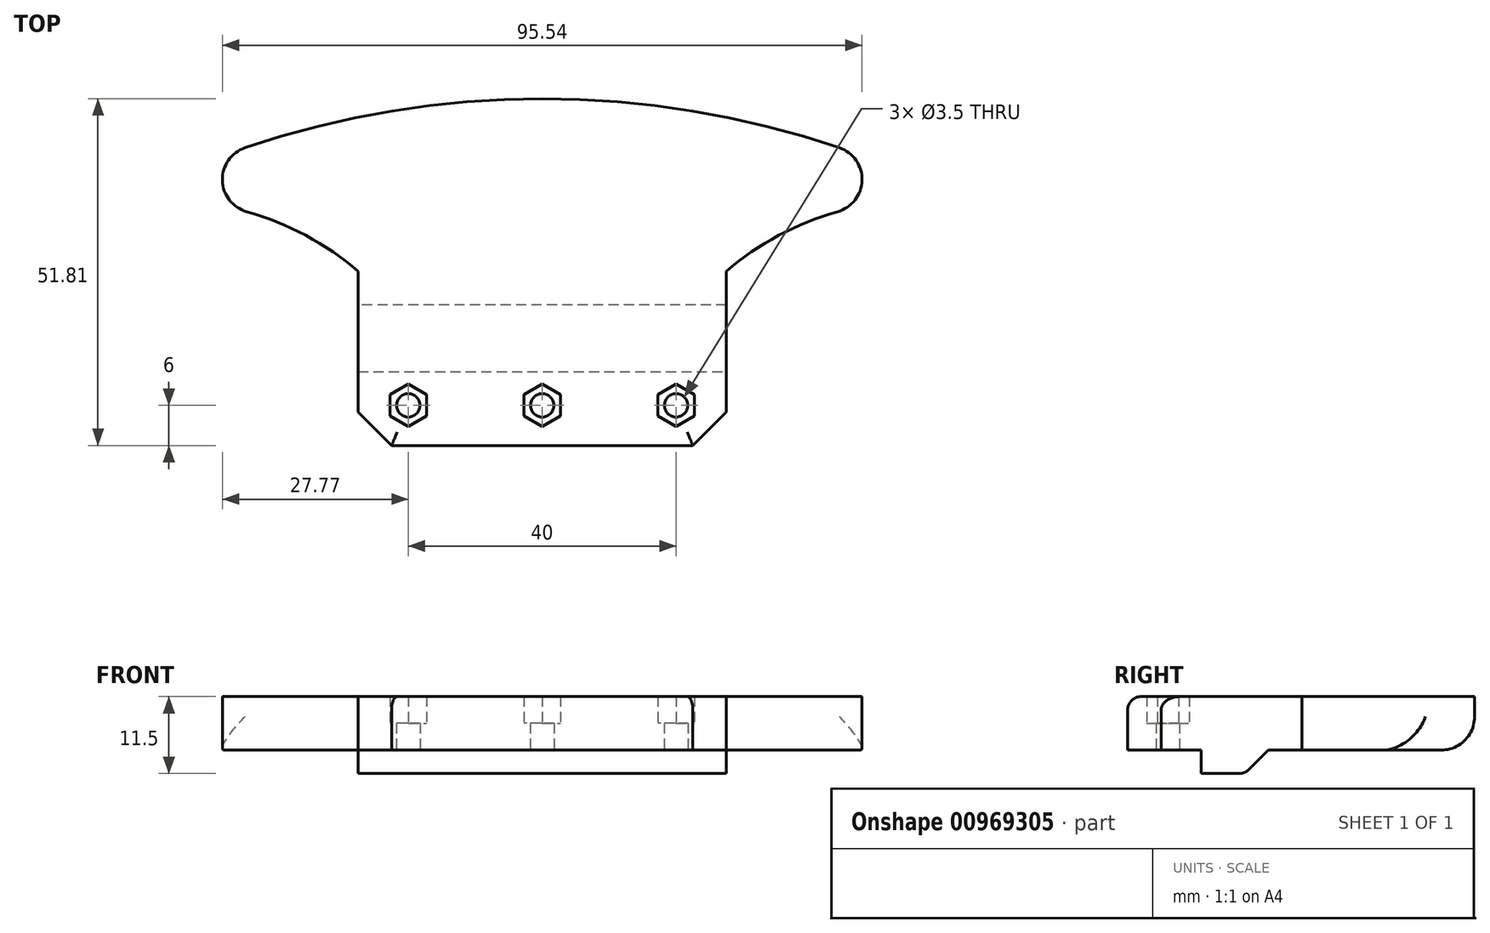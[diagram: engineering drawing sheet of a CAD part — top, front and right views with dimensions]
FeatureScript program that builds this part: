
annotation { "Feature Type Name" : "Feature", "Feature Type Description" : "" }
export const myFeature = defineFeature(function(context is Context, id is Id, definition is map)
    precondition{}
    {
        {
            assignVariable(context, id + "F0", {"name" : "TotalHeight", "anyValue" : 8});
        }
        {
            var Q0;
            Q0=qCreatedBy(makeId("Top.planeOp"),FACE);
            var sketch = newSketch(context, id + "F1", { "sketchPlane" : qUnion([Q0])});
            skCircle(sketch, "E0", {"center": v(0, -10) * mm, "radius": 1.75 * mm});
            skCircle(sketch, "E1", {"center": v(-20, -10) * mm, "radius": 1.75 * mm});
            skCircle(sketch, "E2", {"center": v(20, -10) * mm, "radius": 1.75 * mm});
            skLineSegment(sketch, "E3", {"start": v(0, -10) * mm, "end": v(-20, -10) * mm, "construction": true});
            skLineSegment(sketch, "E4", {"start": v(0, -10) * mm, "end": v(20, -10) * mm, "construction": true});
            skLineSegment(sketch, "E5", {"start": v(-27.5, 0) * mm, "end": v(27.5, 0) * mm});
            skLineSegment(sketch, "E6", {"start": v(-27.5, 0) * mm, "end": v(-27.5, -16) * mm});
            skLineSegment(sketch, "E7", {"start": v(-27.5, -16) * mm, "end": v(27.5, -16) * mm});
            skLineSegment(sketch, "E8", {"start": v(27.5, -16) * mm, "end": v(27.5, 0) * mm});
            skLineSegment(sketch, "E9", {"start": v(-27.5, -5) * mm, "end": v(27.5, -5) * mm});
            skCircle(sketch, "E10.cCircle", {"center": v(0, -10) * mm, "radius": 2.75 * mm, "construction": true});
            skLineSegment(sketch, "E10.0", {"start": v(-2.75, -11.59) * mm, "end": v(-2.75, -8.41) * mm});
            skLineSegment(sketch, "E10.1", {"start": v(-2.75, -8.41) * mm, "end": v(0, -6.82) * mm});
            skLineSegment(sketch, "E10.2", {"start": v(0, -6.82) * mm, "end": v(2.75, -8.41) * mm});
            skLineSegment(sketch, "E10.3", {"start": v(2.75, -8.41) * mm, "end": v(2.75, -11.59) * mm});
            skLineSegment(sketch, "E10.4", {"start": v(2.75, -11.59) * mm, "end": v(0, -13.18) * mm});
            skLineSegment(sketch, "E10.5", {"start": v(0, -13.18) * mm, "end": v(-2.75, -11.59) * mm});
            skPoint(sketch, "E10.0.midPoint", {"position": v(-2.75, -10) * mm});
            skCircle(sketch, "E11.cCircle", {"center": v(20, -10) * mm, "radius": 2.75 * mm, "construction": true});
            skLineSegment(sketch, "E11.0", {"start": v(17.25, -11.59) * mm, "end": v(17.25, -8.41) * mm});
            skLineSegment(sketch, "E11.1", {"start": v(17.25, -8.41) * mm, "end": v(20, -6.82) * mm});
            skLineSegment(sketch, "E11.2", {"start": v(20, -6.82) * mm, "end": v(22.75, -8.41) * mm});
            skLineSegment(sketch, "E11.3", {"start": v(22.75, -8.41) * mm, "end": v(22.75, -11.59) * mm});
            skLineSegment(sketch, "E11.4", {"start": v(22.75, -11.59) * mm, "end": v(20, -13.18) * mm});
            skLineSegment(sketch, "E11.5", {"start": v(20, -13.18) * mm, "end": v(17.25, -11.59) * mm});
            skPoint(sketch, "E11.0.midPoint", {"position": v(17.25, -10) * mm});
            skCircle(sketch, "E12.cCircle", {"center": v(-20, -10) * mm, "radius": 2.75 * mm, "construction": true});
            skLineSegment(sketch, "E12.0", {"start": v(-22.75, -11.59) * mm, "end": v(-22.75, -8.41) * mm});
            skLineSegment(sketch, "E12.1", {"start": v(-22.75, -8.41) * mm, "end": v(-20, -6.82) * mm});
            skLineSegment(sketch, "E12.2", {"start": v(-20, -6.82) * mm, "end": v(-17.25, -8.41) * mm});
            skLineSegment(sketch, "E12.3", {"start": v(-17.25, -8.41) * mm, "end": v(-17.25, -11.59) * mm});
            skLineSegment(sketch, "E12.4", {"start": v(-17.25, -11.59) * mm, "end": v(-20, -13.18) * mm});
            skLineSegment(sketch, "E12.5", {"start": v(-20, -13.18) * mm, "end": v(-22.75, -11.59) * mm});
            skPoint(sketch, "E12.0.midPoint", {"position": v(-22.75, -10) * mm});
            skLineSegment(sketch, "E13", {"start": v(-27.5, 0) * mm, "end": v(-27.5, 10) * mm});
            skLineSegment(sketch, "E14", {"start": v(27.5, 0) * mm, "end": v(27.5, 10) * mm});
            skArc(sketch, "E15", {"start": v(-27.5, 10) * mm, "mid": v(-45.16, 19.2) * mm, "end": v(-65.08, 19.48) * mm});
            skArc(sketch, "E16.MirrorCS", {"start": v(27.5, 10) * mm, "mid": v(45.16, 19.2) * mm, "end": v(65.08, 19.48) * mm});
            skArc(sketch, "E17", {"start": v(65.08, 19.48) * mm, "mid": v(0, 35.8) * mm, "end": v(-65.08, 19.48) * mm});
            skSolve(sketch);
        }
        {
            var Q0;
            Q0=makeQuery(id+"F1.imprint","IMPRINT",FACE,{"disambiguationData":[TD([[makeQuery(id+"F1.imprint","IMPRINT",EDGE,{"derivedFrom":sQuery(id+"F1.wireOp",EDGE,"E5")}),1.0]])]});
            var Q1;
            {var subQ0=sQuery(id+"F1.wireOp",EDGE,"E5");Q1=makeQuery(id+"F1.imprint","IMPRINT",FACE,{"disambiguationData":[TD([[makeQuery(id+"F1.imprint","IMPRINT",EDGE,{"derivedFrom":subQ0}),-1.0]])]});}
            var Q2;
            {var subQ0=sQuery(id+"F1.wireOp",EDGE,"E7");Q2=makeQuery(id+"F1.imprint","IMPRINT",FACE,{"disambiguationData":[TD([[makeQuery(id+"F1.imprint","IMPRINT",EDGE,{"derivedFrom":subQ0}),1.0]])]});}
            var Q3;
            Q3=makeQuery(id+"F1.imprint","IMPRINT",FACE,{"disambiguationData":[TD([[makeQuery(id+"F1.imprint","IMPRINT",EDGE,{"derivedFrom":sQuery(id+"F1.wireOp",EDGE,"aea27d31-c2ea-4929-b87c-4423526370fa.0")}),1.0]])]});
            var Q4;
            Q4=makeQuery(id+"F1.imprint","IMPRINT",FACE,{"disambiguationData":[TD([[makeQuery(id+"F1.imprint","IMPRINT",EDGE,{"derivedFrom":sQuery(id+"F1.wireOp",EDGE,"E10.0")}),1.0]])]});
            extrude(context, id + "F2", {"entities" : qUnion([Q0, Q1, Q2, Q3, Q4]), "depth" : (getVariable(context, 'TotalHeight')) * mm, "offsetDistance" : 25 * mm});
        }
        {
            var Q0;
            Q0=makeQuery(id+"F1.imprint","IMPRINT",FACE,{"disambiguationData":[TD([[makeQuery(id+"F1.imprint","IMPRINT",EDGE,{"derivedFrom":sQuery(id+"F1.wireOp",EDGE,"E1")}),-1.0]])]});
            var Q1;
            Q1=makeQuery(id+"F1.imprint","IMPRINT",FACE,{"disambiguationData":[TD([[makeQuery(id+"F1.imprint","IMPRINT",EDGE,{"derivedFrom":sQuery(id+"F1.wireOp",EDGE,"E0")}),-1.0]])]});
            var Q2;
            Q2=makeQuery(id+"F1.imprint","IMPRINT",FACE,{"disambiguationData":[TD([[makeQuery(id+"F1.imprint","IMPRINT",EDGE,{"derivedFrom":sQuery(id+"F1.wireOp",EDGE,"E2")}),-1.0]])]});
            extrude(context, id + "F3", {"entities" : qUnion([Q0, Q1, Q2]), "operationType" : NewBodyOperationType.ADD, "depth" : (getVariable(context, 'TotalHeight') - 4) * mm, "offsetDistance" : 25 * mm});
        }
        {
            var Q0;
            {var subQ0=sQuery(id+"F1.wireOp",EDGE,"E5");Q0=makeQuery(id+"F1.imprint","IMPRINT",FACE,{"disambiguationData":[TD([[makeQuery(id+"F1.imprint","IMPRINT",EDGE,{"derivedFrom":subQ0}),-1.0]])]});}
            extrude(context, id + "F4", {"entities" : qUnion([Q0]), "operationType" : NewBodyOperationType.ADD, "oppositeDirection" : true, "depth" : 3.5 * mm, "offsetDistance" : 25 * mm});
        }
        {
            var Q0;
            Q0=makeQuery(id+"F2.opExtrude","SWEPT_EDGE",EDGE,{"disambiguationData":[OSD([sQuery(id+"F1.wireOp",EDGE,"E6"),sQuery(id+"F1.wireOp",EDGE,"E7")])]});
            var Q1;
            Q1=makeQuery(id+"F2.opExtrude","SWEPT_EDGE",EDGE,{"disambiguationData":[OSD([sQuery(id+"F1.wireOp",EDGE,"E7"),sQuery(id+"F1.wireOp",EDGE,"E8")])]});
            var Q2;
            Q2=makeQuery(id+"F4.opExtrude","CAP_EDGE",EDGE,{"disambiguationData":[OSD([sQuery(id+"F1.wireOp",EDGE,"E5")])],"isStart":true});
            chamfer(context, id + "F5", {"entities" : qUnion([Q0, Q1, Q2]), "width" : 5 * mm, "tangentPropagation" : true});
        }
        {
            var Q0;
            Q0=makeQuery(id+"F2.opExtrude","CAP_EDGE",EDGE,{"disambiguationData":[OSD([sQuery(id+"F1.wireOp",EDGE,"E17")])],"isStart":true});
            var Q1;
            Q1=makeQuery(id+"F2.opExtrude","SWEPT_EDGE",EDGE,{"disambiguationData":[OSD([sQuery(id+"F1.wireOp",EDGE,"E15"),sQuery(id+"F1.wireOp",EDGE,"E17")])]});
            var Q2;
            Q2=makeQuery(id+"F2.opExtrude","SWEPT_EDGE",EDGE,{"disambiguationData":[OSD([sQuery(id+"F1.wireOp",EDGE,"E16.MirrorCS"),sQuery(id+"F1.wireOp",EDGE,"E17")])]});
            fillet(context, id + "F6", {"entities" : qUnion([Q0, Q1, Q2]), "radius" : 5 * mm, "tangentPropagation" : true, "allowEdgeOverflow" : false});
        }
        {
            var Q0;
            Q0=makeQuery(id+"F2.opExtrude","CAP_EDGE",EDGE,{"disambiguationData":[OSD([sQuery(id+"F1.wireOp",EDGE,"RsASE5nG-dPRU-RCI8-2qOx-PYFyHNF62bff")])],"isStart":true});
            var Q1;
            Q1=makeQuery(id+"F2.opExtrude","CAP_EDGE",EDGE,{"disambiguationData":[OSD([sQuery(id+"F1.wireOp",EDGE,"RsASE5nG-dPRU-RCI8-2qOx-PYFyHNF62bff")])],"isStart":false});
            var Q2;
            Q2=makeQuery(id+"F2.opExtrude","CAP_EDGE",EDGE,{"disambiguationData":[OSD([sQuery(id+"F1.wireOp",EDGE,"a3d60bbd-cd07-4952-b1fc-f427da875249.1")])],"isStart":true});
            var Q3;
            Q3=makeQuery(id+"F2.opExtrude","CAP_EDGE",EDGE,{"disambiguationData":[OSD([sQuery(id+"F1.wireOp",EDGE,"a3d60bbd-cd07-4952-b1fc-f427da875249.3")])],"isStart":false});
            var Q4;
            Q4=makeQuery(id+"F2.opExtrude","CAP_EDGE",EDGE,{"disambiguationData":[OSD([sQuery(id+"F1.wireOp",EDGE,"E7")])],"isStart":false});
            var Q5;
            {var subQ0=sQuery(id+"F1.wireOp",EDGE,"E7");var subQ1=sQuery(id+"F1.wireOp",EDGE,"E6");Q5=makeQuery(id+"F5.opChamfer","BLEND_EDGE",EDGE,{"blendedFrom":[makeQuery(id+"F4.boolean.opBoolean","MERGE",EDGE,{"derivedFrom":[makeQuery(id+"F2.opExtrude","SWEPT_EDGE",EDGE,{"disambiguationData":[OSD([subQ1,subQ0])]}),makeQuery(id+"F4.opExtrude","SWEPT_EDGE",EDGE,{"disambiguationData":[OSD([subQ1,subQ0])]})]}),makeQuery(id+"F2.opExtrude","CAP_FACE",FACE,{"disambiguationData":[OSD([subQ1,subQ0,sQuery(id+"F1.wireOp",EDGE,"E8"),sQuery(id+"F1.wireOp",EDGE,"aea27d31-c2ea-4929-b87c-4423526370fa.0"),sQuery(id+"F1.wireOp",EDGE,"aea27d31-c2ea-4929-b87c-4423526370fa.1"),sQuery(id+"F1.wireOp",EDGE,"aea27d31-c2ea-4929-b87c-4423526370fa.2"),sQuery(id+"F1.wireOp",EDGE,"aea27d31-c2ea-4929-b87c-4423526370fa.3"),sQuery(id+"F1.wireOp",EDGE,"aea27d31-c2ea-4929-b87c-4423526370fa.4"),sQuery(id+"F1.wireOp",EDGE,"aea27d31-c2ea-4929-b87c-4423526370fa.5"),sQuery(id+"F1.wireOp",EDGE,"E10.0"),sQuery(id+"F1.wireOp",EDGE,"E10.1"),sQuery(id+"F1.wireOp",EDGE,"E10.2"),sQuery(id+"F1.wireOp",EDGE,"E10.3"),sQuery(id+"F1.wireOp",EDGE,"E10.4"),sQuery(id+"F1.wireOp",EDGE,"E10.5"),sQuery(id+"F1.wireOp",EDGE,"E11.0"),sQuery(id+"F1.wireOp",EDGE,"E11.1"),sQuery(id+"F1.wireOp",EDGE,"E11.2"),sQuery(id+"F1.wireOp",EDGE,"E11.3"),sQuery(id+"F1.wireOp",EDGE,"E11.4"),sQuery(id+"F1.wireOp",EDGE,"E11.5"),sQuery(id+"F1.wireOp",EDGE,"RsASE5nG-dPRU-RCI8-2qOx-PYFyHNF62bff"),sQuery(id+"F1.wireOp",EDGE,"eb05861e-74fa-4697-aaf9-f4aa3c3135bf0.MirrorCS"),sQuery(id+"F1.wireOp",EDGE,"gBohGyNM-2VbG-c7K3-CVnN-0ivdIRm1ajVN"),sQuery(id+"F1.wireOp",EDGE,"a3d60bbd-cd07-4952-b1fc-f427da875249.0"),sQuery(id+"F1.wireOp",EDGE,"a3d60bbd-cd07-4952-b1fc-f427da875249.1"),sQuery(id+"F1.wireOp",EDGE,"a3d60bbd-cd07-4952-b1fc-f427da875249.2"),sQuery(id+"F1.wireOp",EDGE,"a3d60bbd-cd07-4952-b1fc-f427da875249.3")])],"isStart":false})],"blendedInto":[makeQuery(id+"F2.opExtrude","CAP_FACE",FACE,{"disambiguationData":[OSD([subQ1,subQ0,sQuery(id+"F1.wireOp",EDGE,"E8"),sQuery(id+"F1.wireOp",EDGE,"aea27d31-c2ea-4929-b87c-4423526370fa.0"),sQuery(id+"F1.wireOp",EDGE,"aea27d31-c2ea-4929-b87c-4423526370fa.1"),sQuery(id+"F1.wireOp",EDGE,"aea27d31-c2ea-4929-b87c-4423526370fa.2"),sQuery(id+"F1.wireOp",EDGE,"aea27d31-c2ea-4929-b87c-4423526370fa.3"),sQuery(id+"F1.wireOp",EDGE,"aea27d31-c2ea-4929-b87c-4423526370fa.4"),sQuery(id+"F1.wireOp",EDGE,"aea27d31-c2ea-4929-b87c-4423526370fa.5"),sQuery(id+"F1.wireOp",EDGE,"E10.0"),sQuery(id+"F1.wireOp",EDGE,"E10.1"),sQuery(id+"F1.wireOp",EDGE,"E10.2"),sQuery(id+"F1.wireOp",EDGE,"E10.3"),sQuery(id+"F1.wireOp",EDGE,"E10.4"),sQuery(id+"F1.wireOp",EDGE,"E10.5"),sQuery(id+"F1.wireOp",EDGE,"E11.0"),sQuery(id+"F1.wireOp",EDGE,"E11.1"),sQuery(id+"F1.wireOp",EDGE,"E11.2"),sQuery(id+"F1.wireOp",EDGE,"E11.3"),sQuery(id+"F1.wireOp",EDGE,"E11.4"),sQuery(id+"F1.wireOp",EDGE,"E11.5"),sQuery(id+"F1.wireOp",EDGE,"RsASE5nG-dPRU-RCI8-2qOx-PYFyHNF62bff"),sQuery(id+"F1.wireOp",EDGE,"eb05861e-74fa-4697-aaf9-f4aa3c3135bf0.MirrorCS"),sQuery(id+"F1.wireOp",EDGE,"gBohGyNM-2VbG-c7K3-CVnN-0ivdIRm1ajVN"),sQuery(id+"F1.wireOp",EDGE,"a3d60bbd-cd07-4952-b1fc-f427da875249.0"),sQuery(id+"F1.wireOp",EDGE,"a3d60bbd-cd07-4952-b1fc-f427da875249.1"),sQuery(id+"F1.wireOp",EDGE,"a3d60bbd-cd07-4952-b1fc-f427da875249.2"),sQuery(id+"F1.wireOp",EDGE,"a3d60bbd-cd07-4952-b1fc-f427da875249.3")])],"isStart":false})]});}
            var Q6;
            {var subQ0=sQuery(id+"F1.wireOp",EDGE,"E8");var subQ1=sQuery(id+"F1.wireOp",EDGE,"E7");Q6=makeQuery(id+"F5.opChamfer","BLEND_EDGE",EDGE,{"blendedFrom":[makeQuery(id+"F4.boolean.opBoolean","MERGE",EDGE,{"derivedFrom":[makeQuery(id+"F2.opExtrude","SWEPT_EDGE",EDGE,{"disambiguationData":[OSD([subQ1,subQ0])]}),makeQuery(id+"F4.opExtrude","SWEPT_EDGE",EDGE,{"disambiguationData":[OSD([subQ1,subQ0])]})]}),makeQuery(id+"F2.opExtrude","CAP_FACE",FACE,{"disambiguationData":[OSD([sQuery(id+"F1.wireOp",EDGE,"E6"),subQ1,subQ0,sQuery(id+"F1.wireOp",EDGE,"aea27d31-c2ea-4929-b87c-4423526370fa.0"),sQuery(id+"F1.wireOp",EDGE,"aea27d31-c2ea-4929-b87c-4423526370fa.1"),sQuery(id+"F1.wireOp",EDGE,"aea27d31-c2ea-4929-b87c-4423526370fa.2"),sQuery(id+"F1.wireOp",EDGE,"aea27d31-c2ea-4929-b87c-4423526370fa.3"),sQuery(id+"F1.wireOp",EDGE,"aea27d31-c2ea-4929-b87c-4423526370fa.4"),sQuery(id+"F1.wireOp",EDGE,"aea27d31-c2ea-4929-b87c-4423526370fa.5"),sQuery(id+"F1.wireOp",EDGE,"E10.0"),sQuery(id+"F1.wireOp",EDGE,"E10.1"),sQuery(id+"F1.wireOp",EDGE,"E10.2"),sQuery(id+"F1.wireOp",EDGE,"E10.3"),sQuery(id+"F1.wireOp",EDGE,"E10.4"),sQuery(id+"F1.wireOp",EDGE,"E10.5"),sQuery(id+"F1.wireOp",EDGE,"E11.0"),sQuery(id+"F1.wireOp",EDGE,"E11.1"),sQuery(id+"F1.wireOp",EDGE,"E11.2"),sQuery(id+"F1.wireOp",EDGE,"E11.3"),sQuery(id+"F1.wireOp",EDGE,"E11.4"),sQuery(id+"F1.wireOp",EDGE,"E11.5"),sQuery(id+"F1.wireOp",EDGE,"RsASE5nG-dPRU-RCI8-2qOx-PYFyHNF62bff"),sQuery(id+"F1.wireOp",EDGE,"eb05861e-74fa-4697-aaf9-f4aa3c3135bf0.MirrorCS"),sQuery(id+"F1.wireOp",EDGE,"gBohGyNM-2VbG-c7K3-CVnN-0ivdIRm1ajVN"),sQuery(id+"F1.wireOp",EDGE,"a3d60bbd-cd07-4952-b1fc-f427da875249.0"),sQuery(id+"F1.wireOp",EDGE,"a3d60bbd-cd07-4952-b1fc-f427da875249.1"),sQuery(id+"F1.wireOp",EDGE,"a3d60bbd-cd07-4952-b1fc-f427da875249.2"),sQuery(id+"F1.wireOp",EDGE,"a3d60bbd-cd07-4952-b1fc-f427da875249.3")])],"isStart":false})],"blendedInto":[makeQuery(id+"F2.opExtrude","CAP_FACE",FACE,{"disambiguationData":[OSD([sQuery(id+"F1.wireOp",EDGE,"E6"),subQ1,subQ0,sQuery(id+"F1.wireOp",EDGE,"aea27d31-c2ea-4929-b87c-4423526370fa.0"),sQuery(id+"F1.wireOp",EDGE,"aea27d31-c2ea-4929-b87c-4423526370fa.1"),sQuery(id+"F1.wireOp",EDGE,"aea27d31-c2ea-4929-b87c-4423526370fa.2"),sQuery(id+"F1.wireOp",EDGE,"aea27d31-c2ea-4929-b87c-4423526370fa.3"),sQuery(id+"F1.wireOp",EDGE,"aea27d31-c2ea-4929-b87c-4423526370fa.4"),sQuery(id+"F1.wireOp",EDGE,"aea27d31-c2ea-4929-b87c-4423526370fa.5"),sQuery(id+"F1.wireOp",EDGE,"E10.0"),sQuery(id+"F1.wireOp",EDGE,"E10.1"),sQuery(id+"F1.wireOp",EDGE,"E10.2"),sQuery(id+"F1.wireOp",EDGE,"E10.3"),sQuery(id+"F1.wireOp",EDGE,"E10.4"),sQuery(id+"F1.wireOp",EDGE,"E10.5"),sQuery(id+"F1.wireOp",EDGE,"E11.0"),sQuery(id+"F1.wireOp",EDGE,"E11.1"),sQuery(id+"F1.wireOp",EDGE,"E11.2"),sQuery(id+"F1.wireOp",EDGE,"E11.3"),sQuery(id+"F1.wireOp",EDGE,"E11.4"),sQuery(id+"F1.wireOp",EDGE,"E11.5"),sQuery(id+"F1.wireOp",EDGE,"RsASE5nG-dPRU-RCI8-2qOx-PYFyHNF62bff"),sQuery(id+"F1.wireOp",EDGE,"eb05861e-74fa-4697-aaf9-f4aa3c3135bf0.MirrorCS"),sQuery(id+"F1.wireOp",EDGE,"gBohGyNM-2VbG-c7K3-CVnN-0ivdIRm1ajVN"),sQuery(id+"F1.wireOp",EDGE,"a3d60bbd-cd07-4952-b1fc-f427da875249.0"),sQuery(id+"F1.wireOp",EDGE,"a3d60bbd-cd07-4952-b1fc-f427da875249.1"),sQuery(id+"F1.wireOp",EDGE,"a3d60bbd-cd07-4952-b1fc-f427da875249.2"),sQuery(id+"F1.wireOp",EDGE,"a3d60bbd-cd07-4952-b1fc-f427da875249.3")])],"isStart":false})]});}
            var Q7;
            Q7=makeQuery(id+"F5.opChamfer","BLEND_EDGE",EDGE,{"blendedFrom":[makeQuery(id+"F4.opExtrude","CAP_EDGE",EDGE,{"disambiguationData":[OSD([sQuery(id+"F1.wireOp",EDGE,"E5")])],"isStart":true}),makeQuery(id+"F2.opExtrude","SWEPT_FACE",FACE,{"disambiguationData":[OSD([sQuery(id+"F1.wireOp",EDGE,"eb05861e-74fa-4697-aaf9-f4aa3c3135bf0.MirrorCS")])]})],"blendedInto":[makeQuery(id+"F2.opExtrude","SWEPT_FACE",FACE,{"disambiguationData":[OSD([sQuery(id+"F1.wireOp",EDGE,"eb05861e-74fa-4697-aaf9-f4aa3c3135bf0.MirrorCS")])]})]});
            var Q8;
            Q8=makeQuery(id+"F5.opChamfer","BLEND_EDGE",EDGE,{"blendedFrom":[makeQuery(id+"F4.opExtrude","CAP_EDGE",EDGE,{"disambiguationData":[OSD([sQuery(id+"F1.wireOp",EDGE,"E5")])],"isStart":true}),makeQuery(id+"F2.opExtrude","SWEPT_FACE",FACE,{"disambiguationData":[OSD([sQuery(id+"F1.wireOp",EDGE,"RsASE5nG-dPRU-RCI8-2qOx-PYFyHNF62bff")])]})],"blendedInto":[makeQuery(id+"F2.opExtrude","SWEPT_FACE",FACE,{"disambiguationData":[OSD([sQuery(id+"F1.wireOp",EDGE,"RsASE5nG-dPRU-RCI8-2qOx-PYFyHNF62bff")])]})]});
            var Q9;
            Q9=makeQuery(id+"F5.opChamfer","BLEND_EDGE",EDGE,{"blendedFrom":[makeQuery(id+"F4.opExtrude","CAP_EDGE",EDGE,{"disambiguationData":[OSD([sQuery(id+"F1.wireOp",EDGE,"E5")])],"isStart":true}),makeQuery(id+"F2.opExtrude","SWEPT_FACE",FACE,{"disambiguationData":[OSD([sQuery(id+"F1.wireOp",EDGE,"a3d60bbd-cd07-4952-b1fc-f427da875249.2")])]})],"blendedInto":[makeQuery(id+"F2.opExtrude","SWEPT_FACE",FACE,{"disambiguationData":[OSD([sQuery(id+"F1.wireOp",EDGE,"a3d60bbd-cd07-4952-b1fc-f427da875249.2")])]})]});
            var Q10;
            {var subQ0=sQuery(id+"F1.wireOp",EDGE,"E5");Q10=makeQuery(id+"F5.opChamfer","BLEND_EDGE",EDGE,{"blendedFrom":[makeQuery(id+"F4.opExtrude","CAP_EDGE",EDGE,{"disambiguationData":[OSD([subQ0])],"isStart":true}),makeQuery(id+"F4.opExtrude","CAP_FACE",FACE,{"disambiguationData":[OSD([subQ0,sQuery(id+"F1.wireOp",EDGE,"E6"),sQuery(id+"F1.wireOp",EDGE,"E7"),sQuery(id+"F1.wireOp",EDGE,"E8"),sQuery(id+"F1.wireOp",EDGE,"E9"),sQuery(id+"F1.wireOp",EDGE,"82qEuTwf-rWpJ-iMl8-XhDT-ZZMlZaatkq3s.left"),sQuery(id+"F1.wireOp",EDGE,"82qEuTwf-rWpJ-iMl8-XhDT-ZZMlZaatkq3s.right")])],"isStart":false})],"blendedInto":[makeQuery(id+"F4.opExtrude","CAP_FACE",FACE,{"disambiguationData":[OSD([subQ0,sQuery(id+"F1.wireOp",EDGE,"E6"),sQuery(id+"F1.wireOp",EDGE,"E7"),sQuery(id+"F1.wireOp",EDGE,"E8"),sQuery(id+"F1.wireOp",EDGE,"E9"),sQuery(id+"F1.wireOp",EDGE,"82qEuTwf-rWpJ-iMl8-XhDT-ZZMlZaatkq3s.left"),sQuery(id+"F1.wireOp",EDGE,"82qEuTwf-rWpJ-iMl8-XhDT-ZZMlZaatkq3s.right")])],"isStart":false})]});}
            fillet(context, id + "F7", {"entities" : qUnion([Q0, Q1, Q2, Q3, Q4, Q5, Q6, Q7, Q8, Q9, Q10]), "radius" : 2 * mm, "tangentPropagation" : true, "allowEdgeOverflow" : false});
        }
    });
